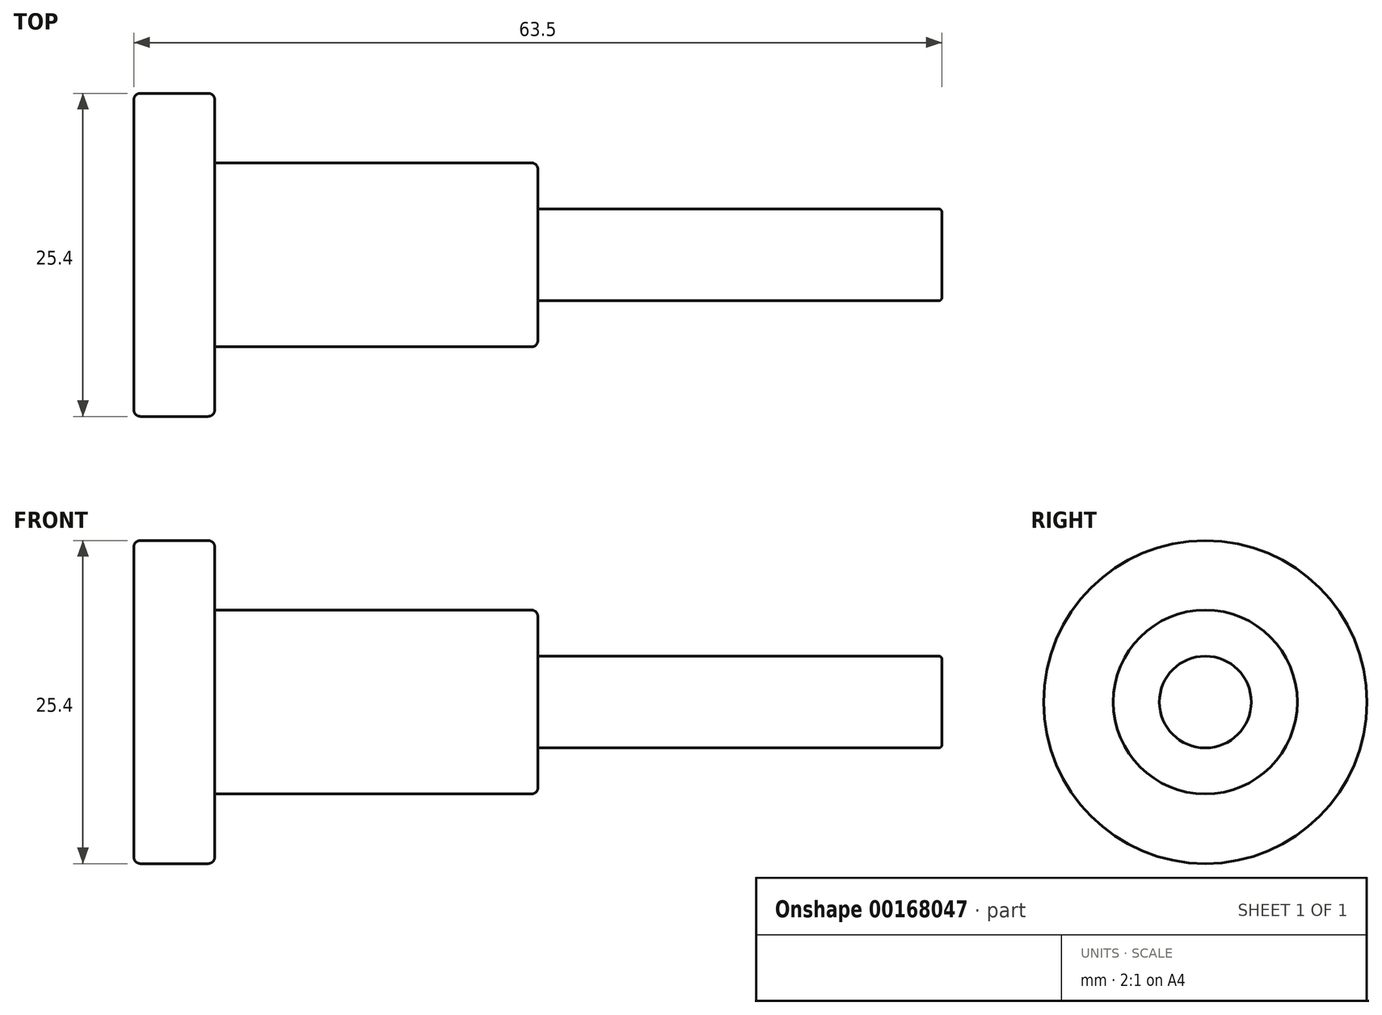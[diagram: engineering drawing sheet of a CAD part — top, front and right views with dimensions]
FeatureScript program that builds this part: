
annotation { "Feature Type Name" : "Feature", "Feature Type Description" : "" }
export const myFeature = defineFeature(function(context is Context, id is Id, definition is map)
    precondition{}
    {
        {
            var Q0;
            Q0=qCreatedBy(makeId("Right.planeOp"),FACE);
            var sketch = newSketch(context, id + "F0", { "sketchPlane" : qUnion([Q0])});
            skCircle(sketch, "E0", {"center": v(0, 0) * mm, "radius": 12.7 * mm});
            skSolve(sketch);
        }
        {
            var Q0;
            Q0 = qSketchRegion(id + "F0", true);
            extrude(context, id + "F1", {"entities" : qUnion([Q0]), "oppositeDirection" : true, "depth" : 6.35 * mm});
        }
        {
            var Q0;
            Q0=qCreatedBy(makeId("Right.planeOp"),FACE);
            var sketch = newSketch(context, id + "F2", { "sketchPlane" : qUnion([Q0])});
            skCircle(sketch, "E1", {"center": v(0, 0) * mm, "radius": 7.23 * mm});
            skSolve(sketch);
        }
        {
            var Q0;
            Q0 = qSketchRegion(id + "F2", true);
            extrude(context, id + "F3", {"entities" : qUnion([Q0]), "operationType" : NewBodyOperationType.ADD, "depth" : 25.4 * mm});
        }
        {
            var Q0;
            Q0=makeQuery(id+"F3.opExtrude","CAP_FACE",FACE,{"disambiguationData":[OSD([sQuery(id+"F2.wireOp",EDGE,"E1")])],"isStart":false});
            var sketch = newSketch(context, id + "F4", { "sketchPlane" : qUnion([Q0])});
            skCircle(sketch, "E2", {"center": v(0, 0) * mm, "radius": 3.6 * mm});
            skSolve(sketch);
        }
        {
            var Q0;
            Q0 = qSketchRegion(id + "F4", true);
            var Q1;
            Q1=sQuery(id+"F4.wireOp",EDGE,"E2");
            extrude(context, id + "F5", {"entities" : qUnion([Q0]), "operationType" : NewBodyOperationType.ADD, "surfaceEntities" : qUnion([Q1]), "depth" : 31.75 * mm});
        }
        {
            var Q0;
            Q0=makeQuery(id+"F1.opExtrude","CAP_EDGE",EDGE,{"disambiguationData":[OSD([sQuery(id+"F0.wireOp",EDGE,"E0")])],"isStart":false});
            fillet(context, id + "F6", {"entities" : qUnion([Q0]), "radius" : 0.5 * mm, "tangentPropagation" : true, "allowEdgeOverflow" : false});
        }
        {
            var Q0;
            Q0=makeQuery(id+"F1.opExtrude","CAP_EDGE",EDGE,{"disambiguationData":[OSD([sQuery(id+"F0.wireOp",EDGE,"E0")])],"isStart":true});
            fillet(context, id + "F7", {"entities" : qUnion([Q0]), "radius" : 0.5 * mm, "tangentPropagation" : true, "allowEdgeOverflow" : false});
        }
        {
            var Q0;
            Q0=makeQuery(id+"F3.opExtrude","CAP_EDGE",EDGE,{"disambiguationData":[OSD([sQuery(id+"F2.wireOp",EDGE,"E1")])],"isStart":false});
            fillet(context, id + "F8", {"entities" : qUnion([Q0]), "radius" : 0.5 * mm, "tangentPropagation" : true, "allowEdgeOverflow" : false});
        }
        {
            var Q0;
            Q0=makeQuery(id+"F5.opExtrude","CAP_EDGE",EDGE,{"disambiguationData":[OSD([sQuery(id+"F4.wireOp",EDGE,"E2")])],"isStart":false});
            fillet(context, id + "F9", {"entities" : qUnion([Q0]), "radius" : 0.25 * mm, "tangentPropagation" : true, "allowEdgeOverflow" : false});
        }
    });
